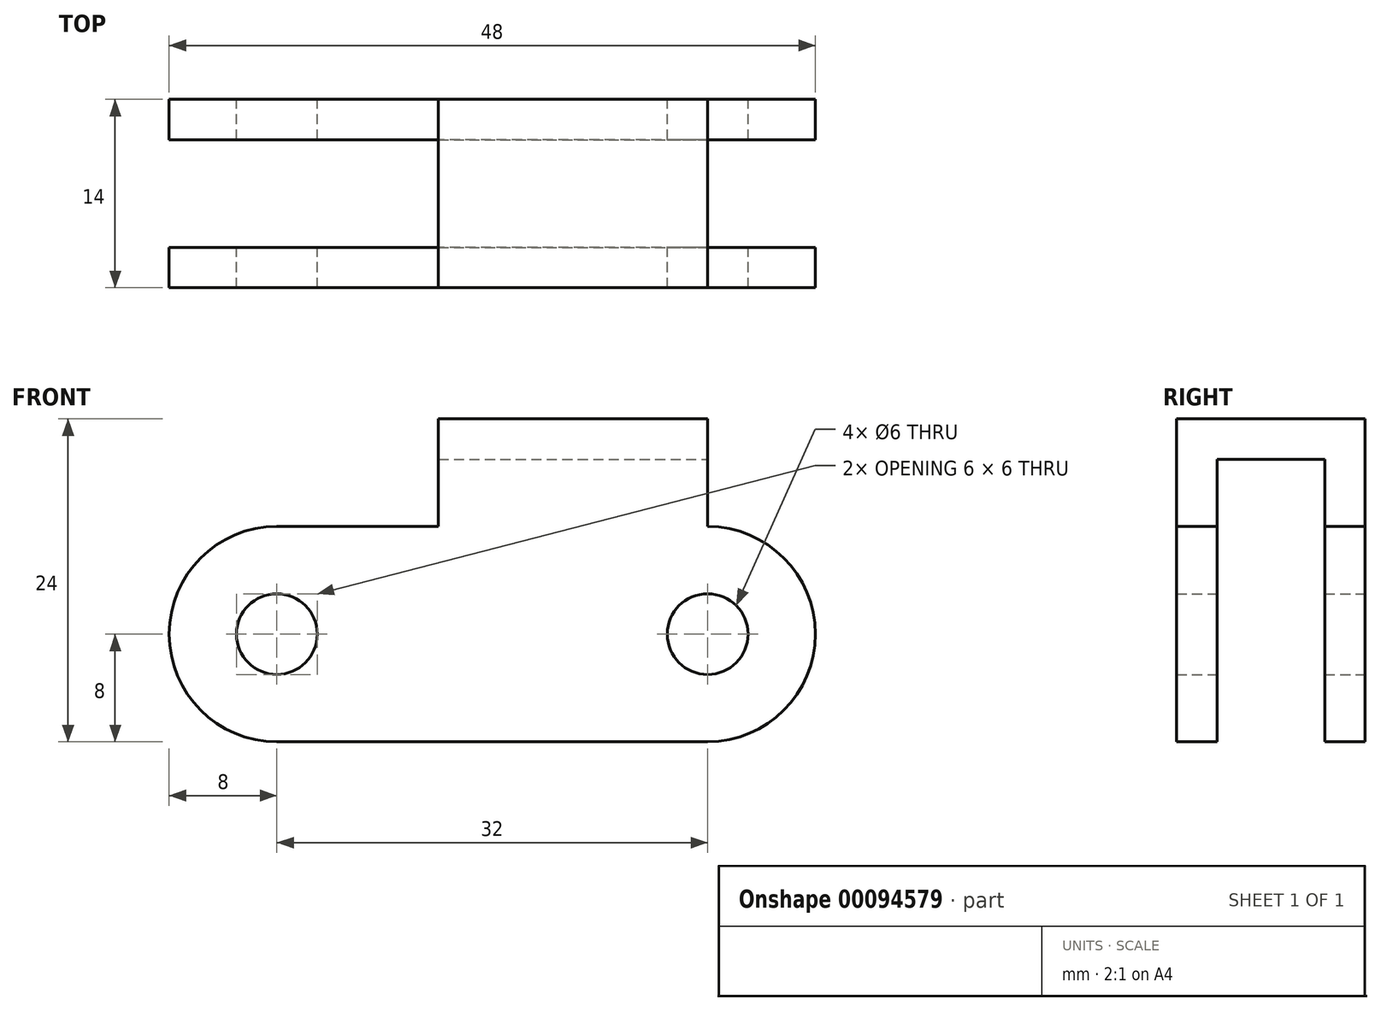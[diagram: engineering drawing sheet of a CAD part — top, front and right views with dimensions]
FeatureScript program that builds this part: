
annotation { "Feature Type Name" : "Feature", "Feature Type Description" : "" }
export const myFeature = defineFeature(function(context is Context, id is Id, definition is map)
    precondition{}
    {
        {
            var Q0;
            Q0=qCreatedBy(makeId("Front.planeOp"),FACE);
            var sketch = newSketch(context, id + "F0", { "sketchPlane" : qUnion([Q0])});
            skLineSegment(sketch, "E0", {"start": v(-32, 0) * mm, "end": v(0, 0) * mm, "construction": true});
            skArc(sketch, "E1.0.startCap", {"start": v(-32, -8) * mm, "mid": v(-40, 0) * mm, "end": v(-32, 8) * mm});
            skArc(sketch, "E1.0.endCap", {"start": v(0, 8) * mm, "mid": v(8, 0) * mm, "end": v(0, -8) * mm});
            skLineSegment(sketch, "E1.0.left", {"start": v(-32, 8) * mm, "end": v(0, 8) * mm});
            skLineSegment(sketch, "E1.0.right", {"start": v(-32, -8) * mm, "end": v(0, -8) * mm});
            skCircle(sketch, "E2", {"center": v(-32, 0) * mm, "radius": 3 * mm});
            skCircle(sketch, "E3", {"center": v(0, 0) * mm, "radius": 3 * mm});
            skLineSegment(sketch, "E4.bottom", {"start": v(0, 8) * mm, "end": v(-20, 8) * mm});
            skLineSegment(sketch, "E4.top", {"start": v(0, 16) * mm, "end": v(-20, 16) * mm});
            skLineSegment(sketch, "E4.left", {"start": v(0, 8) * mm, "end": v(0, 16) * mm});
            skLineSegment(sketch, "E4.right", {"start": v(-20, 8) * mm, "end": v(-20, 16) * mm});
            skSolve(sketch);
        }
        {
            var Q0;
            Q0 = qSketchRegion(id + "F0", true);
            extrude(context, id + "F1", {"entities" : qUnion([Q0]), "endBound" : BoundingType.SYMMETRIC, "depth" : 14 * mm});
        }
        {
            var Q0;
            Q0=qCreatedBy(makeId("Right.planeOp"),FACE);
            var sketch = newSketch(context, id + "F2", { "sketchPlane" : qUnion([Q0])});
            skLineSegment(sketch, "E5.bottom", {"start": v(4, -13) * mm, "end": v(-4, -13) * mm});
            skLineSegment(sketch, "E5.top", {"start": v(4, 13) * mm, "end": v(-4, 13) * mm});
            skLineSegment(sketch, "E5.left", {"start": v(4, -13) * mm, "end": v(4, 13) * mm});
            skLineSegment(sketch, "E5.right", {"start": v(-4, -13) * mm, "end": v(-4, 13) * mm});
            skPoint(sketch, "E5.middle", {"position": v(0, 0) * mm});
            skSolve(sketch);
        }
        {
            var Q0;
            Q0=makeQuery(id+"F2.imprint","IMPRINT",FACE,{"disambiguationData":[TD([[makeQuery(id+"F2.imprint","IMPRINT",EDGE,{"derivedFrom":sQuery(id+"F2.wireOp",EDGE,"E5.bottom")}),-1.0]])]});
            extrude(context, id + "F3", {"entities" : qUnion([Q0]), "operationType" : NewBodyOperationType.REMOVE, "endBound" : BoundingType.SYMMETRIC, "oppositeDirection" : true, "depth" : 104.85 * mm});
        }
    });
